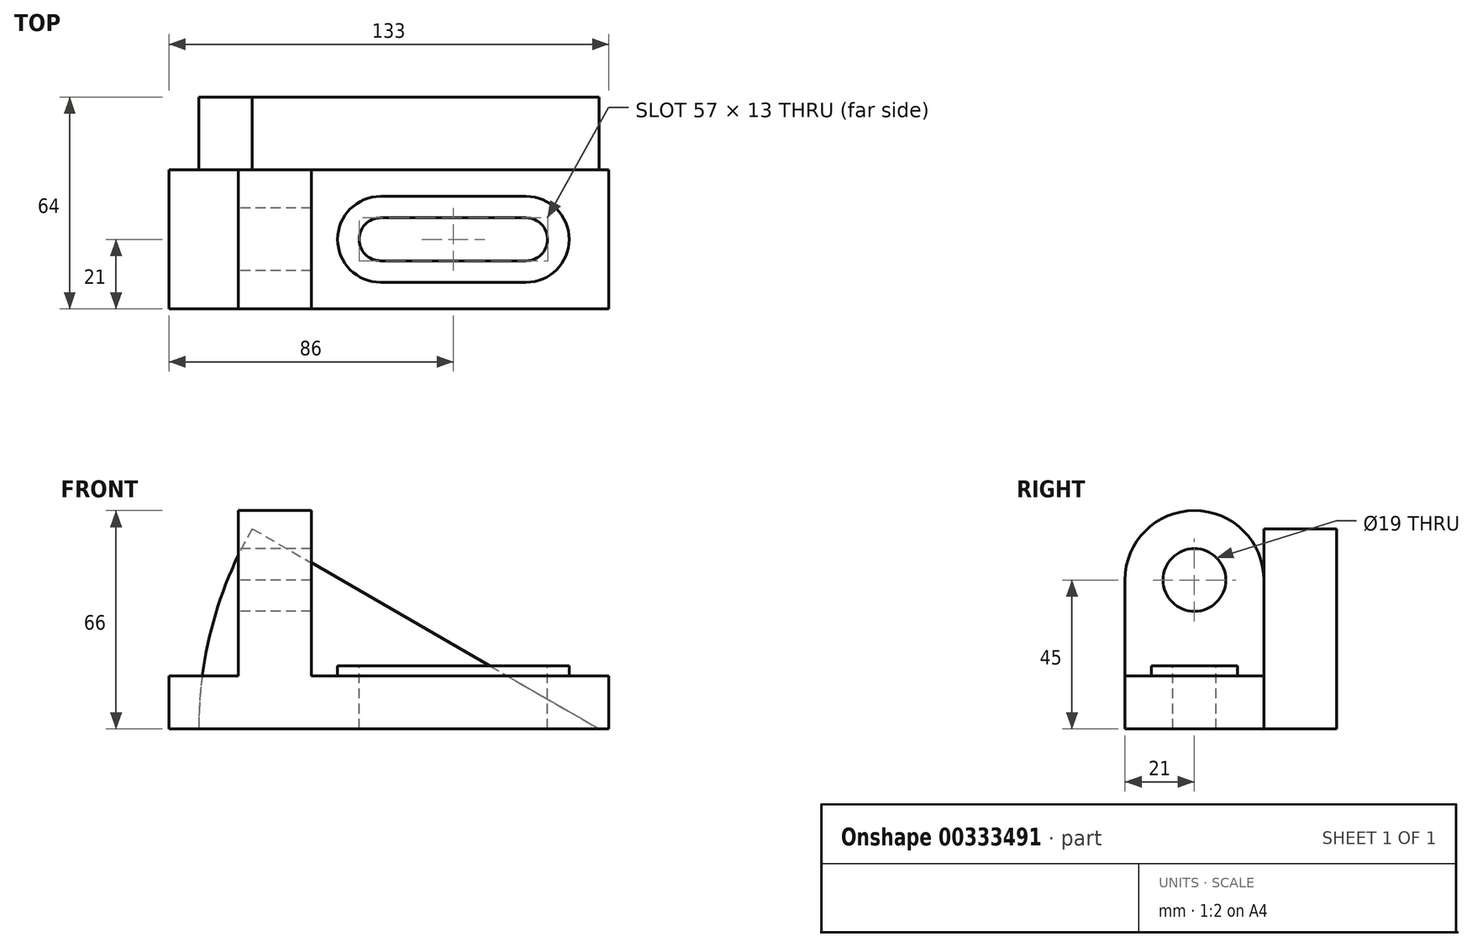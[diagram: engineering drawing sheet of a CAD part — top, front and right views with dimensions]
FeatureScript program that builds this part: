
annotation { "Feature Type Name" : "Feature", "Feature Type Description" : "" }
export const myFeature = defineFeature(function(context is Context, id is Id, definition is map)
    precondition{}
    {
        {
            var Q0;
            Q0=qCreatedBy(makeId("Front.planeOp"),FACE);
            var sketch = newSketch(context, id + "F0", { "sketchPlane" : qUnion([Q0])});
            skLineSegment(sketch, "E0", {"start": v(0, 0) * mm, "end": v(0, 16) * mm});
            skLineSegment(sketch, "E1", {"start": v(0, 16) * mm, "end": v(21, 16) * mm});
            skLineSegment(sketch, "E2", {"start": v(21, 16) * mm, "end": v(21, 66) * mm});
            skLineSegment(sketch, "E3", {"start": v(21, 66) * mm, "end": v(43, 66) * mm});
            skLineSegment(sketch, "E4", {"start": v(43, 66) * mm, "end": v(43, 16) * mm});
            skLineSegment(sketch, "E5", {"start": v(43, 16) * mm, "end": v(133, 16) * mm});
            skLineSegment(sketch, "E6", {"start": v(133, 16) * mm, "end": v(133, 0) * mm});
            skLineSegment(sketch, "E7", {"start": v(133, 0) * mm, "end": v(0, 0) * mm});
            skSolve(sketch);
        }
        {
            var Q0;
            Q0 = qSketchRegion(id + "F0", true);
            extrude(context, id + "F1", {"entities" : qUnion([Q0]), "depth" : 42 * mm});
        }
        {
            var Q0;
            Q0=makeQuery(id+"F1.opExtrude","SWEPT_FACE",FACE,{"disambiguationData":[OSD([sQuery(id+"F0.wireOp",EDGE,"E2")])]});
            var sketch = newSketch(context, id + "F2", { "sketchPlane" : qUnion([Q0])});
            skLineSegment(sketch, "E8", {"start": v(0, 45) * mm, "end": v(0, 16) * mm});
            skLineSegment(sketch, "E9", {"start": v(0, 16) * mm, "end": v(42, 16) * mm});
            skLineSegment(sketch, "E10", {"start": v(42, 16) * mm, "end": v(42, 45) * mm});
            skArc(sketch, "E11", {"start": v(42, 45) * mm, "mid": v(21, 66) * mm, "end": v(0, 45) * mm});
            skSolve(sketch);
        }
        {
            var Q0;
            {var subQ0=sQuery(id+"F2.wireOp",EDGE,"E11");var subQ1=sQuery(id+"F0.wireOp",EDGE,"E2");var subQ2=makeQuery(id+"F1.opExtrude","CAP_EDGE",EDGE,{"disambiguationData":[OSD([subQ1])],"isStart":true});var subQ3=makeQuery(id+"F2.imprint","INTERSECT",VERTEX,{"derivedFrom":[subQ2,sQuery(id+"F2.wireOp",EDGE,"E8"),subQ0]});Q0=makeQuery(id+"F2.imprint","IMPRINT",FACE,{"disambiguationData":[TD([[makeQuery(id+"F2.imprint","IMPRINT",EDGE,{"disambiguationData":[TD([[subQ3,1.0]])],"derivedFrom":subQ0}),-1.0]])]});}
            var Q1;
            {var subQ0=sQuery(id+"F2.wireOp",EDGE,"E11");var subQ1=sQuery(id+"F0.wireOp",EDGE,"E2");var subQ2=makeQuery(id+"F1.opExtrude","CAP_EDGE",EDGE,{"disambiguationData":[OSD([subQ1])],"isStart":false});var subQ3=makeQuery(id+"F2.imprint","INTERSECT",VERTEX,{"derivedFrom":[subQ2,sQuery(id+"F2.wireOp",EDGE,"E10"),subQ0]});Q1=makeQuery(id+"F2.imprint","IMPRINT",FACE,{"disambiguationData":[TD([[makeQuery(id+"F2.imprint","IMPRINT",EDGE,{"disambiguationData":[TD([[subQ3,-1.0]])],"derivedFrom":subQ0}),-1.0]])]});}
            extrude(context, id + "F3", {"entities" : qUnion([Q0, Q1]), "operationType" : NewBodyOperationType.REMOVE, "endBound" : BoundingType.THROUGH_ALL, "oppositeDirection" : true, "depth" : 25 * mm});
        }
        {
            var Q0;
            Q0=makeQuery(id+"F1.opExtrude","SWEPT_FACE",FACE,{"disambiguationData":[OSD([sQuery(id+"F0.wireOp",EDGE,"E2")])]});
            var sketch = newSketch(context, id + "F4", { "sketchPlane" : qUnion([Q0])});
            skCircle(sketch, "E12", {"center": v(21, 45) * mm, "radius": 9.5 * mm});
            skSolve(sketch);
        }
        {
            var Q0;
            Q0 = qSketchRegion(id + "F4", true);
            extrude(context, id + "F5", {"entities" : qUnion([Q0]), "operationType" : NewBodyOperationType.REMOVE, "endBound" : BoundingType.THROUGH_ALL, "oppositeDirection" : true, "depth" : 25 * mm});
        }
        {
            var Q0;
            Q0=makeQuery(id+"F1.opExtrude","SWEPT_FACE",FACE,{"disambiguationData":[OSD([sQuery(id+"F0.wireOp",EDGE,"E5")])]});
            var sketch = newSketch(context, id + "F6", { "sketchPlane" : qUnion([Q0])});
            skLineSegment(sketch, "E13", {"start": v(64, -8) * mm, "end": v(108, -8) * mm});
            skLineSegment(sketch, "E14", {"start": v(64, -34) * mm, "end": v(108, -34) * mm});
            skArc(sketch, "E15", {"start": v(64, -8) * mm, "mid": v(51, -21) * mm, "end": v(64, -34) * mm});
            skArc(sketch, "E16", {"start": v(108, -34) * mm, "mid": v(121, -21) * mm, "end": v(108, -8) * mm});
            skSolve(sketch);
        }
        {
            var Q0;
            Q0 = qSketchRegion(id + "F6", true);
            extrude(context, id + "F7", {"entities" : qUnion([Q0]), "operationType" : NewBodyOperationType.ADD, "depth" : 3 * mm});
        }
        {
            var Q0;
            Q0=qCreatedBy(makeId("Front.planeOp"),FACE);
            var sketch = newSketch(context, id + "F8", { "sketchPlane" : qUnion([Q0])});
            skLineSegment(sketch, "E17.bottom", {"start": v(9, 0) * mm, "end": v(130, 0) * mm});
            skArc(sketch, "E18", {"start": v(25.21, 60.5) * mm, "mid": v(13.12, 31.32) * mm, "end": v(9, 0) * mm});
            skLineSegment(sketch, "E19", {"start": v(25.21, 60.5) * mm, "end": v(130, 0) * mm});
            skPoint(sketch, "E17.left.end.orphan", {"position": v(0, 58.71) * mm});
            skSolve(sketch);
        }
        {
            var Q0;
            Q0=makeQuery(id+"F8.imprint","IMPRINT",FACE,{"disambiguationData":[TD([[makeQuery(id+"F8.imprint","IMPRINT",EDGE,{"derivedFrom":sQuery(id+"F8.wireOp",EDGE,"E17.bottom")}),1.0]])]});
            extrude(context, id + "F9", {"entities" : qUnion([Q0]), "operationType" : NewBodyOperationType.ADD, "oppositeDirection" : true, "depth" : 22 * mm});
        }
        {
            var Q0;
            Q0=makeQuery(id+"F7.opExtrude","CAP_FACE",FACE,{"disambiguationData":[OSD([sQuery(id+"F6.wireOp",EDGE,"E13"),sQuery(id+"F6.wireOp",EDGE,"E14"),sQuery(id+"F6.wireOp",EDGE,"E15"),sQuery(id+"F6.wireOp",EDGE,"E16")])],"isStart":false});
            var sketch = newSketch(context, id + "F10", { "sketchPlane" : qUnion([Q0])});
            skLineSegment(sketch, "E20", {"start": v(64, -14.5) * mm, "end": v(108, -14.5) * mm});
            skLineSegment(sketch, "E21", {"start": v(64, -27.5) * mm, "end": v(108, -27.5) * mm});
            skArc(sketch, "E22", {"start": v(64, -14.5) * mm, "mid": v(57.5, -21) * mm, "end": v(64, -27.5) * mm});
            skArc(sketch, "E23", {"start": v(108, -27.5) * mm, "mid": v(114.5, -21) * mm, "end": v(108, -14.5) * mm});
            skLineSegment(sketch, "E24", {"start": v(51, -21) * mm, "end": v(121, -21) * mm, "construction": true});
            skSolve(sketch);
        }
        {
            var Q0;
            Q0 = qSketchRegion(id + "F10", true);
            extrude(context, id + "F11", {"entities" : qUnion([Q0]), "operationType" : NewBodyOperationType.REMOVE, "oppositeDirection" : true, "depth" : 25 * mm});
        }
    });
